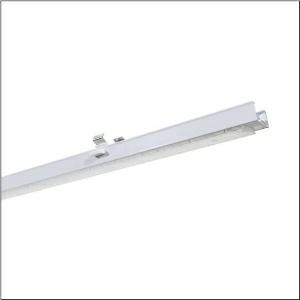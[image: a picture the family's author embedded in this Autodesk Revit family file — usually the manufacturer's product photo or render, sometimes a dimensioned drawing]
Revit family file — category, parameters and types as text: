
# Revit family: trunking_flex_31_51re14mb68b
name_source: partatom
category: Lighting Fixtures
units: mm (PartAtom-declared; Revit-internal decimal feet)

## family parameters
Cut with Voids When Loaded = No
Host = Face
Light Source = No
Part Type = Normal
Room Calculation Point = No
Round Connector Dimension = Use Diameter
Shared = No

## types (1)
- --- (1 x LED, 8000 lm, 50 W, 6500K)
    Apparent Load = 50 VA
    CIE Flux Codes = 72 92 98 99 100
    Color Rendering = 80
    Color Temperature = 6500K
    Default Elevation = 1800 mm
    Description = Trunking Flex 31, luminaire insert, of extruded aluminium section, coated, traffic white (RAL 9016), length: 1.472mm, width: 91mm, height: 53mm, LED rated luminous flux: 8.000lm, light colour: 865, SDCM (Standard Deviation of Colour Matching)MacAdam ≤ 3 SDCM (initial), control gear: ON/OFF Multilumen, with system connector: socket, mains connection: 220..240V, AC, 50/60Hz, rated input power: 50W, luminous flux adjustable on luminaire in four steps (4130/5610/6850/8000lm), connected load according to luminous flux setting (25/34/42/50W), primary light control with lens, of plastic, primary optical cover: cover, of PMMA, light emission: direct distribution, primary light characteristic: asymmetric, protection rating (complete): IP20, insulation class (complete): insulation class I (protective earthing), certification: CE, UKCA, impact resistance: IK02, permissible ambient temperature for indoor applications: -20..+40°C, packaging unit: 1 piece
    Height = 58 mm
    Lamp = 1 x LED
    Lamp Light Flux = 8000 lm
    Lamp Power = 50 W
    Lamp count = 1
    Length = 1472 mm
    Luminous efficacy = 160 lm/W
    Manufacturer = Siteco
    ModVariant = No
    Model = 51RE14MB68B
    Mounting Place = Ceiling
    Mounting Type = Pendant
    Number of Poles = 1
    OnlyDefault = Yes
    Power Factor = 1
    Product Name = Trunking Flex 31
    Product group = luminaire insert | ceiling pendant
    ProductGroupID = 901
    Protection Class = Protection class I
    Protection Degree = IP 20
    RLX_Detail_Level = 1
    RLX_Emergency_Light_Flux = 0 lm
    RLX_Emergency_Type = 0
    RLX_Emergency_Type_DB = No
    RlxData = <blob elided: 21157 chars, md5=76dd9f45>
    Socket = socket
    Standby Power = 0 W
    System Light Flux = 8000 lm
    System Power = 50 W
    Type Comments = factory setting: luminous flux: 100 % | (ON | ON) | 300 mA
    Type Image = l_1266702.jpg
    URL = http://relux.com
    VarID = @adj_065605
    Voltage = 0 V
    Weight = 0.00 kg
    Width = 65 mm

## geometry (parser evidence)
native form markers: Blend x4, Sweep x12
no freeform markers — native parametric forms only
